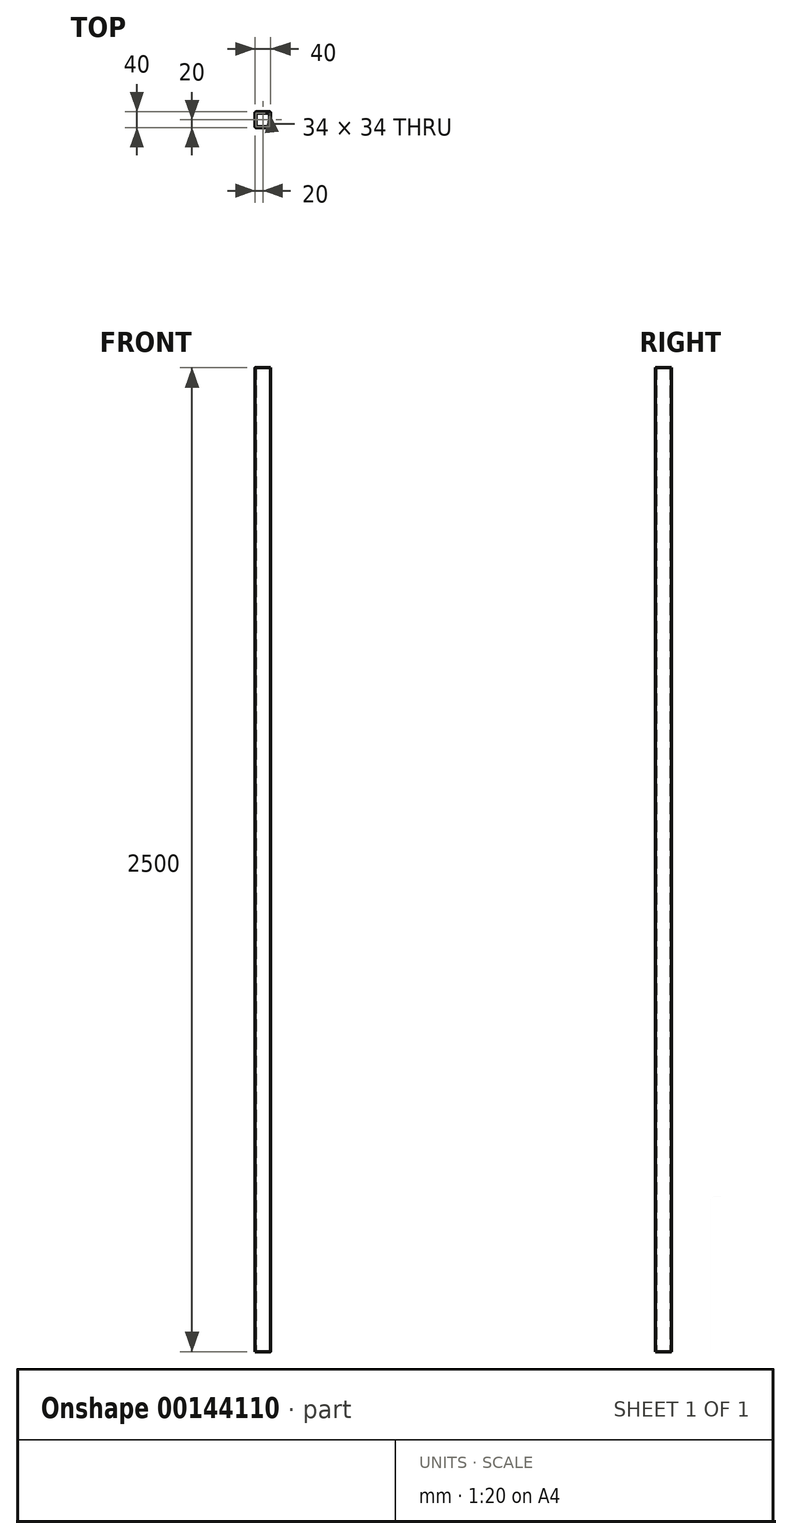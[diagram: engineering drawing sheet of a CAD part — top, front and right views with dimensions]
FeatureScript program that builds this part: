
annotation { "Feature Type Name" : "Feature", "Feature Type Description" : "" }
export const myFeature = defineFeature(function(context is Context, id is Id, definition is map)
    precondition{}
    {
        {
            var Q0;
            Q0=qCreatedBy(makeId("Top.planeOp"),FACE);
            var sketch = newSketch(context, id + "F0", { "sketchPlane" : qUnion([Q0])});
            skLineSegment(sketch, "E0.bottom", {"start": v(17, 20) * mm, "end": v(-17, 20) * mm});
            skLineSegment(sketch, "E0.top", {"start": v(17, -20) * mm, "end": v(-17, -20) * mm});
            skLineSegment(sketch, "E0.left", {"start": v(20, 17) * mm, "end": v(20, -17) * mm});
            skLineSegment(sketch, "E0.right", {"start": v(-20, 17) * mm, "end": v(-20, -17) * mm});
            skPoint(sketch, "E0.middle", {"position": v(0, 0) * mm});
            skPoint(sketch, "E1.visualSharp", {"position": v(-20, 20) * mm});
            skArc(sketch, "E1.filletArc", {"start": v(-17, 20) * mm, "mid": v(-19.12, 19.12) * mm, "end": v(-20, 17) * mm});
            skPoint(sketch, "E2.visualSharp", {"position": v(20, 20) * mm});
            skArc(sketch, "E2.filletArc", {"start": v(20, 17) * mm, "mid": v(19.12, 19.12) * mm, "end": v(17, 20) * mm});
            skPoint(sketch, "E3.visualSharp", {"position": v(20, -20) * mm});
            skArc(sketch, "E3.filletArc", {"start": v(17, -20) * mm, "mid": v(19.12, -19.12) * mm, "end": v(20, -17) * mm});
            skPoint(sketch, "E4.visualSharp", {"position": v(-20, -20) * mm});
            skArc(sketch, "E4.filletArc", {"start": v(-20, -17) * mm, "mid": v(-19.12, -19.12) * mm, "end": v(-17, -20) * mm});
            skLineSegment(sketch, "E5.0", {"start": v(17, 17) * mm, "end": v(-17, 17) * mm});
            skLineSegment(sketch, "E5.1", {"start": v(17, 17) * mm, "end": v(17, -17) * mm});
            skLineSegment(sketch, "E5.2", {"start": v(17, -17) * mm, "end": v(-17, -17) * mm});
            skLineSegment(sketch, "E5.3", {"start": v(-17, 17) * mm, "end": v(-17, -17) * mm});
            skSolve(sketch);
        }
        {
            var Q0;
            Q0=makeQuery(id+"F0.imprint","IMPRINT",FACE,{"disambiguationData":[TD([[makeQuery(id+"F0.imprint","IMPRINT",EDGE,{"derivedFrom":sQuery(id+"F0.wireOp",EDGE,"E0.bottom")}),1.0]])]});
            extrude(context, id + "F1", {"entities" : qUnion([Q0]), "depth" : 2500 * mm});
        }
    });
